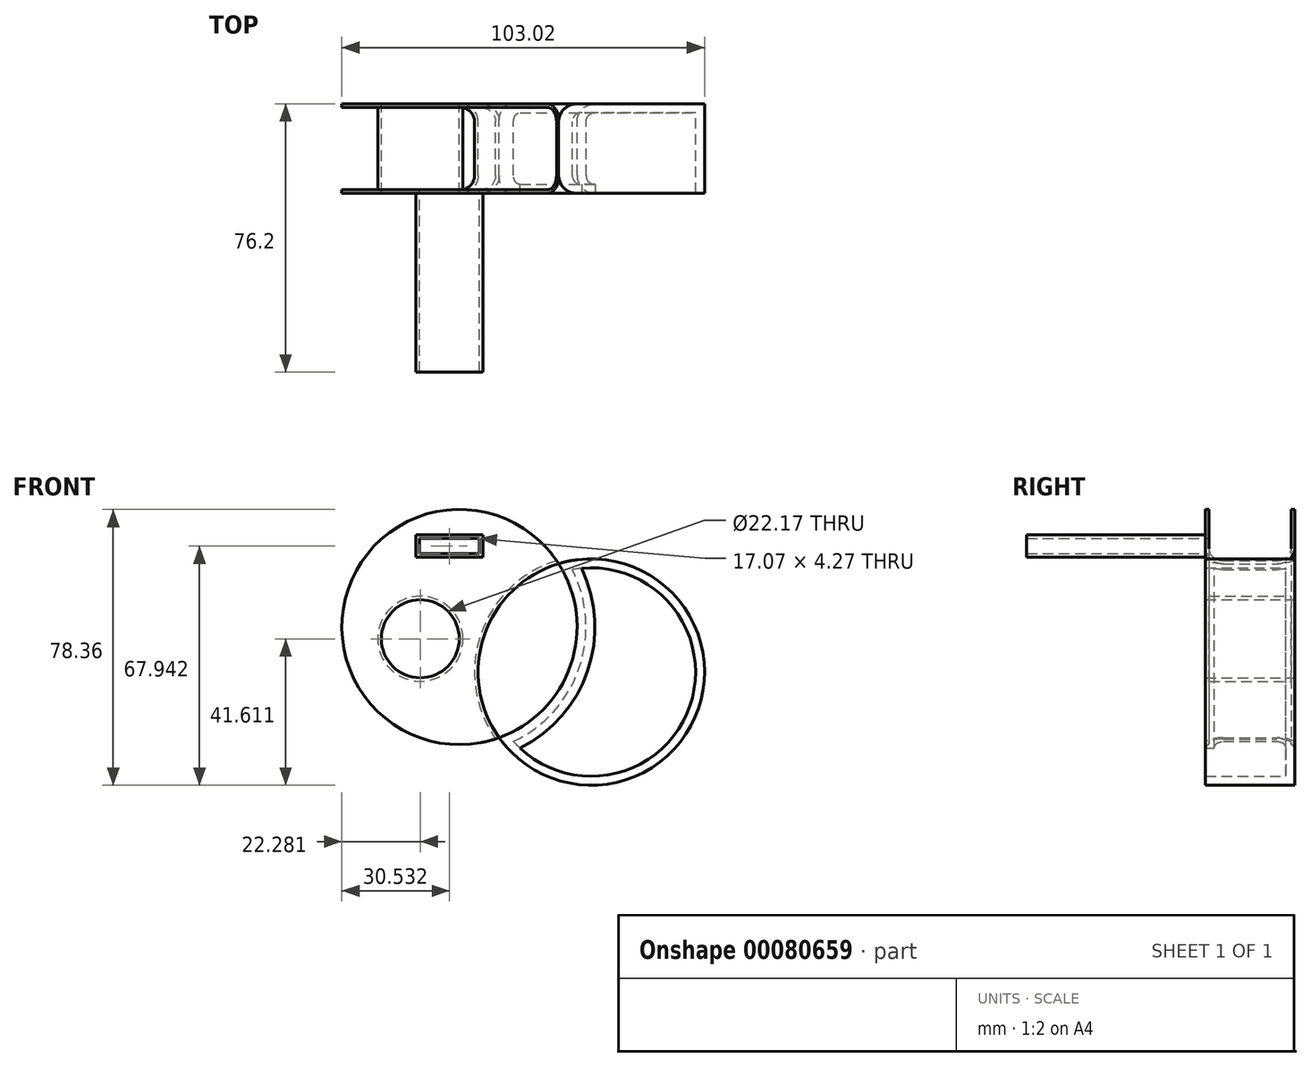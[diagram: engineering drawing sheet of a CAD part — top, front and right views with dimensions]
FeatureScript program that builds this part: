
annotation { "Feature Type Name" : "Feature", "Feature Type Description" : "" }
export const myFeature = defineFeature(function(context is Context, id is Id, definition is map)
    precondition{}
    {
        {
            var Q0;
            Q0=qCreatedBy(makeId("Front.planeOp"),FACE);
            var sketch = newSketch(context, id + "F0", { "sketchPlane" : qUnion([Q0])});
            skCircle(sketch, "E0", {"center": v(-30.22, 42.37) * mm, "radius": 33.4 * mm});
            skCircle(sketch, "E1", {"center": v(7.23, 29.57) * mm, "radius": 32.16 * mm});
            skCircle(sketch, "E2", {"center": v(-41.35, 39.03) * mm, "radius": 11.08 * mm});
            skSolve(sketch);
        }
        {
            var Q0;
            Q0=makeQuery(id+"F0.imprint","IMPRINT",FACE,{"disambiguationData":[TD([[makeQuery(id+"F0.imprint","IMPRINT",EDGE,{"derivedFrom":sQuery(id+"F0.wireOp",EDGE,"E2")}),-1.0]])]});
            var Q1;
            {var subQ0=sQuery(id+"F0.wireOp",EDGE,"E1");var subQ1=sQuery(id+"F0.wireOp",EDGE,"E0");var subQ2=makeQuery(id+"F0.imprint","INTERSECT",VERTEX,{"disambiguationData":[OD(0.0)],"derivedFrom":[subQ1,subQ0]});Q1=makeQuery(id+"F0.imprint","IMPRINT",FACE,{"disambiguationData":[TD([[makeQuery(id+"F0.imprint","IMPRINT",EDGE,{"disambiguationData":[TD([[subQ2,-1.0]])],"derivedFrom":subQ1}),-1.0]])]});}
            extrude(context, id + "F1", {"entities" : qUnion([Q0, Q1]), "depth" : 25.4 * mm});
        }
        {
            var Q0;
            {var subQ0=sQuery(id+"F0.wireOp",EDGE,"E1");var subQ1=sQuery(id+"F0.wireOp",EDGE,"E0");Q0=makeQuery(id+"F1.opExtrude","CAP_EDGE",EDGE,{"disambiguationData":[OSD([subQ0]),TDD([makeQuery(id+"F0.imprint","IMPRINT",EDGE,{"disambiguationData":[TD([[makeQuery(id+"F0.imprint","INTERSECT",VERTEX,{"disambiguationData":[OD(0.0)],"derivedFrom":[subQ1,subQ0]}),1.0]])],"derivedFrom":subQ0})])],"isStart":false});}
            var Q1;
            {var subQ0=sQuery(id+"F0.wireOp",EDGE,"E1");var subQ1=sQuery(id+"F0.wireOp",EDGE,"E0");Q1=makeQuery(id+"F1.opExtrude","CAP_EDGE",EDGE,{"disambiguationData":[OSD([subQ1]),TDD([makeQuery(id+"F0.imprint","IMPRINT",EDGE,{"disambiguationData":[TD([[makeQuery(id+"F0.imprint","INTERSECT",VERTEX,{"disambiguationData":[OD(0.0)],"derivedFrom":[subQ1,subQ0]}),-1.0]])],"derivedFrom":subQ1})])],"isStart":false});}
            var Q2;
            {var subQ0=sQuery(id+"F0.wireOp",EDGE,"E1");var subQ1=sQuery(id+"F0.wireOp",EDGE,"E0");Q2=makeQuery(id+"F1.opExtrude","CAP_EDGE",EDGE,{"disambiguationData":[OSD([subQ0]),TDD([makeQuery(id+"F0.imprint","IMPRINT",EDGE,{"disambiguationData":[TD([[makeQuery(id+"F0.imprint","INTERSECT",VERTEX,{"disambiguationData":[OD(0.0)],"derivedFrom":[subQ1,subQ0]}),1.0]])],"derivedFrom":subQ0})])],"isStart":true});}
            var Q3;
            {var subQ0=sQuery(id+"F0.wireOp",EDGE,"E1");var subQ1=sQuery(id+"F0.wireOp",EDGE,"E0");Q3=makeQuery(id+"F1.opExtrude","CAP_EDGE",EDGE,{"disambiguationData":[OSD([subQ1]),TDD([makeQuery(id+"F0.imprint","IMPRINT",EDGE,{"disambiguationData":[TD([[makeQuery(id+"F0.imprint","INTERSECT",VERTEX,{"disambiguationData":[OD(0.0)],"derivedFrom":[subQ1,subQ0]}),-1.0]])],"derivedFrom":subQ1})])],"isStart":true});}
            fillet(context, id + "F2", {"entities" : qUnion([Q0, Q1, Q2, Q3]), "radius" : 5.08 * mm, "tangentPropagation" : true, "allowEdgeOverflow" : false});
        }
        {
            var Q0;
            Q0=makeQuery(id+"F1.opExtrude","CAP_FACE",FACE,{"disambiguationData":[OSD([sQuery(id+"F0.wireOp",EDGE,"E0"),sQuery(id+"F0.wireOp",EDGE,"E1")])],"isStart":false});
            shell(context, id + "F3", {"entities" : qUnion([Q0]), "thickness" : 2.54 * mm});
        }
        {
            var Q0;
            Q0=makeQuery(id+"F1.opExtrude","CAP_FACE",FACE,{"disambiguationData":[OSD([sQuery(id+"F0.wireOp",EDGE,"E0"),sQuery(id+"F0.wireOp",EDGE,"E1"),sQuery(id+"F0.wireOp",EDGE,"E2")])],"isStart":false});
            var sketch = newSketch(context, id + "F4", { "sketchPlane" : qUnion([Q0])});
            skLineSegment(sketch, "E3.bottom", {"start": v(-42.65, 68.51) * mm, "end": v(-23.55, 68.51) * mm});
            skLineSegment(sketch, "E3.top", {"start": v(-42.65, 62.2) * mm, "end": v(-23.55, 62.2) * mm});
            skLineSegment(sketch, "E3.left", {"start": v(-42.65, 68.51) * mm, "end": v(-42.65, 62.2) * mm});
            skLineSegment(sketch, "E3.right", {"start": v(-23.55, 68.51) * mm, "end": v(-23.55, 62.2) * mm});
            skSolve(sketch);
        }
        {
            var Q0;
            Q0 = qSketchRegion(id + "F4", true);
            extrude(context, id + "F5", {"entities" : qUnion([Q0]), "operationType" : NewBodyOperationType.ADD, "depth" : 50.8 * mm});
        }
        {
            var Q0;
            Q0=makeQuery(id+"F5.opExtrude","CAP_FACE",FACE,{"disambiguationData":[OSD([sQuery(id+"F4.wireOp",EDGE,"E3.bottom"),sQuery(id+"F4.wireOp",EDGE,"E3.top"),sQuery(id+"F4.wireOp",EDGE,"E3.left"),sQuery(id+"F4.wireOp",EDGE,"E3.right")])],"isStart":false});
            var Q1;
            {var subQ0=sQuery(id+"F0.wireOp",EDGE,"E1");var subQ1=sQuery(id+"F0.wireOp",EDGE,"E0");Q1=makeQuery(id+"F1.opExtrude","SWEPT_FACE",FACE,{"disambiguationData":[OSD([subQ1]),TDD([makeQuery(id+"F0.imprint","IMPRINT",EDGE,{"disambiguationData":[TD([[makeQuery(id+"F0.imprint","INTERSECT",VERTEX,{"disambiguationData":[OD(0.0)],"derivedFrom":[subQ1,subQ0]}),1.0]])],"derivedFrom":subQ1})])]});}
            shell(context, id + "F6", {"entities" : qUnion([Q0, Q1]), "thickness" : 1.02 * mm});
        }
    });
